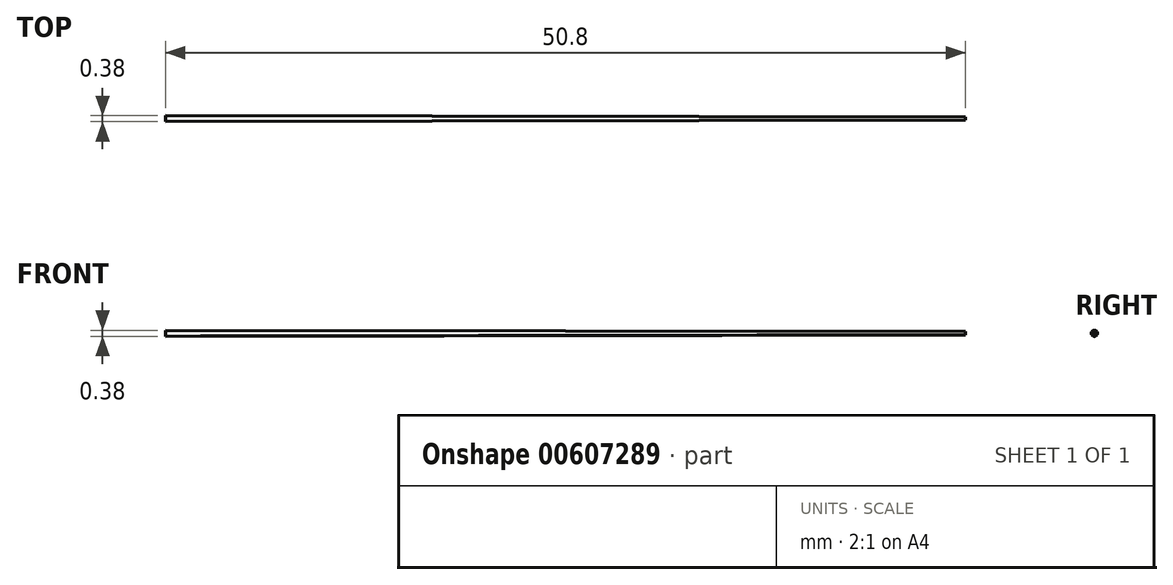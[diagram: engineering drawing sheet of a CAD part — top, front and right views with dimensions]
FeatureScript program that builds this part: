
annotation { "Feature Type Name" : "Feature", "Feature Type Description" : "" }
export const myFeature = defineFeature(function(context is Context, id is Id, definition is map)
    precondition{}
    {
        {
            var Q0;
            Q0=qCreatedBy(makeId("Front.planeOp"),FACE);
            var sketch = newSketch(context, id + "F0", { "sketchPlane" : qUnion([Q0])});
            skLineSegment(sketch, "E0", {"start": v(-26.32, 0) * mm, "end": v(-26.32, 0.2) * mm});
            skLineSegment(sketch, "E1", {"start": v(-26.32, 0.2) * mm, "end": v(24.48, 0.1) * mm});
            skLineSegment(sketch, "E2", {"start": v(24.48, 0.1) * mm, "end": v(24.48, 0) * mm});
            skLineSegment(sketch, "E3", {"start": v(24.48, 0) * mm, "end": v(-26.32, 0) * mm});
            skSolve(sketch);
        }
        {
            var Q0;
            Q0=makeQuery(id+"F0.imprint","IMPRINT",FACE,{"disambiguationData":[TD([[makeQuery(id+"F0.imprint","IMPRINT",EDGE,{"derivedFrom":sQuery(id+"F0.wireOp",EDGE,"E0")}),-1.0]])]});
            var Q1;
            Q1=sQuery(id+"F0.wireOp",EDGE,"E3");
            revolve(context, id + "F1", {"entities" : qUnion([Q0]), "axis" : qUnion([Q1]), "revolveType" : RevolveType.FULL});
        }
    });
